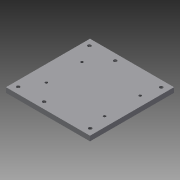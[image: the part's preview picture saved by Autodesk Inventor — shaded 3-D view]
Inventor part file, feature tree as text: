
AUTODESK INVENTOR PART (.ipt)
format: ipt  version: 2015 SP1 (Build 190203100, 203)  size: 101,888 bytes
history: native  units: in
note: dims shown in document units (in); Inventor stores cm internally (conversion verified against a paired STEP export)
features: sketch x3, hole x2, extrude x1, projected_geometry x1
ambient origin geometry x8: Origin, YZ Plane, XZ Plane, XY Plane, X Axis, Y Axis, Z Axis, Center Point
bodies: Solid1 (feature_tree)
feature tree (7):
  extrude  "Extrusion1"  Depth=6.5in
  hole  "Hole1"  [1 undecoded]
  hole  "Hole2"  [1 undecoded]
  sketch  "Sketch2"  dims[d0=6.5in d1=6.5in]
  sketch  "Sketch3"  dims[d2=0.375in d3=0.0in d4=0.45in]
  sketch  "Sketch4"  dims[d5=2.0in d6=3.56in d7=0.5in d8=0.252in d9=0.625in d10=0.635in d11=0.25in d12=0.5635in d13=0.903in d14=0.8108in d15=1.253in d16=4.5in d17=1.872in d18=0.196in d19=0.5in d20=0.507in d21=0.25in d22=0.5635in d23=1.0in d24=0.8108in]
  projected_geometry  "Projected Loop1"
note: 2 required parameter values undecoded (feature->parameter linkage not recoverable at this tier; creation-order binding heuristic only, values carry confidence <= 0.55)
